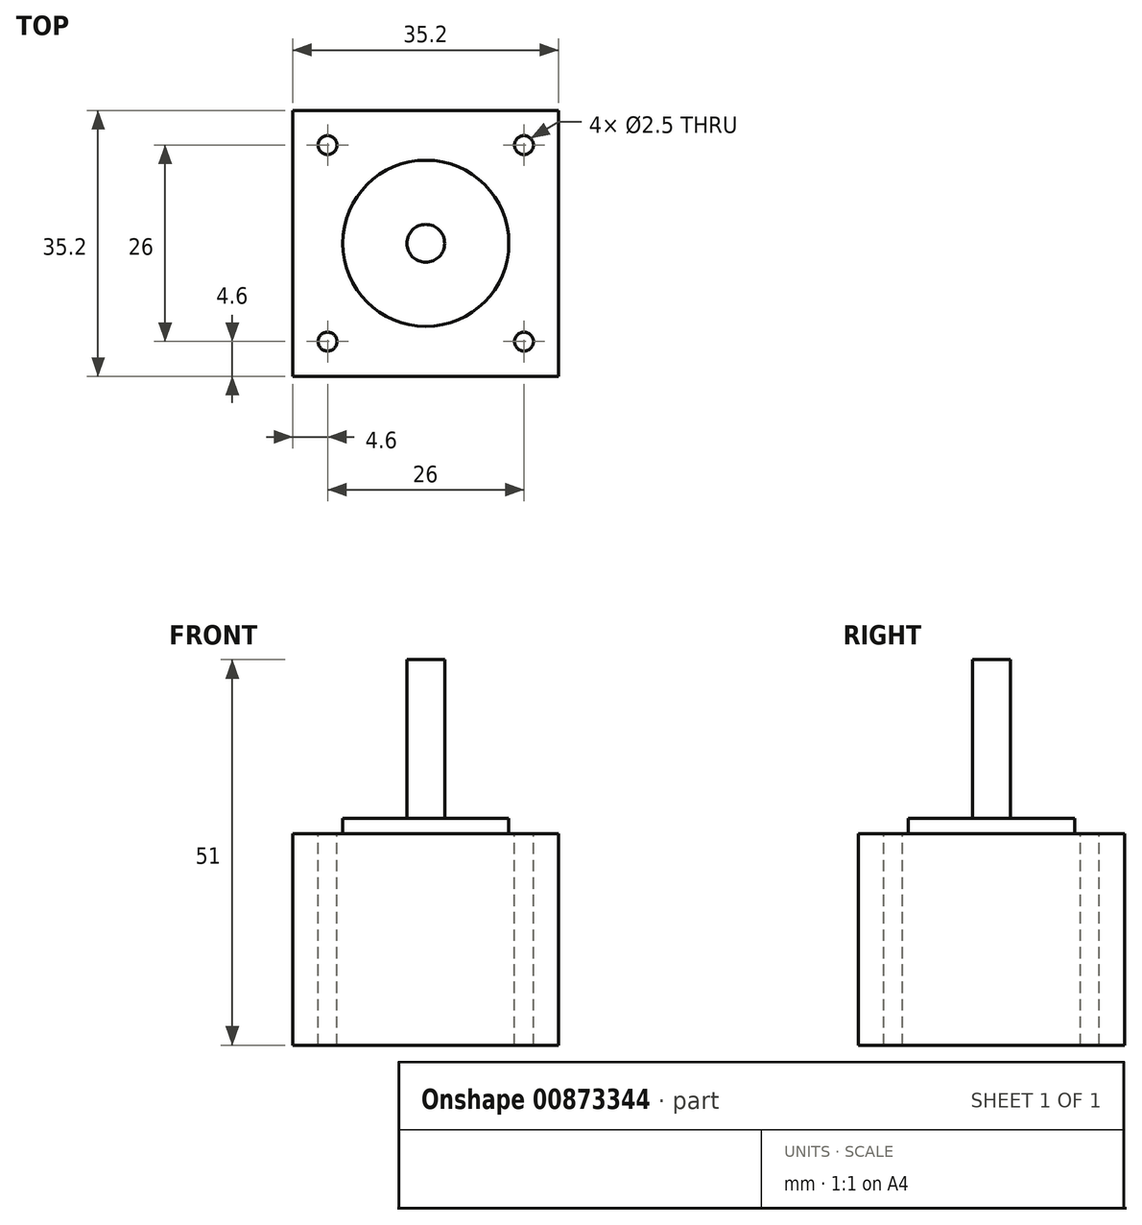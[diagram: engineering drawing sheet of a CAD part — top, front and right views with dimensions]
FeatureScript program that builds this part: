
annotation { "Feature Type Name" : "Feature", "Feature Type Description" : "" }
export const myFeature = defineFeature(function(context is Context, id is Id, definition is map)
    precondition{}
    {
        {
            var Q0;
            Q0=qCreatedBy(makeId("Top.planeOp"),FACE);
            var sketch = newSketch(context, id + "F0", { "sketchPlane" : qUnion([Q0])});
            skLineSegment(sketch, "E0.bottom", {"start": v(17.6, 17.6) * mm, "end": v(-17.6, 17.6) * mm});
            skLineSegment(sketch, "E0.top", {"start": v(17.6, -17.6) * mm, "end": v(-17.6, -17.6) * mm});
            skLineSegment(sketch, "E0.left", {"start": v(17.6, 17.6) * mm, "end": v(17.6, -17.6) * mm});
            skLineSegment(sketch, "E0.right", {"start": v(-17.6, 17.6) * mm, "end": v(-17.6, -17.6) * mm});
            skPoint(sketch, "E0.middle", {"position": v(0, 0) * mm});
            skSolve(sketch);
        }
        {
            var Q0;
            Q0=makeQuery(id+"F0.imprint","IMPRINT",FACE,{"disambiguationData":[TD([[makeQuery(id+"F0.imprint","IMPRINT",EDGE,{"derivedFrom":sQuery(id+"F0.wireOp",EDGE,"E0.bottom")}),1.0]])]});
            extrude(context, id + "F1", {"entities" : qUnion([Q0]), "depth" : 28 * mm, "offsetDistance" : 25 * mm});
        }
        {
            var Q0;
            Q0=makeQuery(id+"F1.opExtrude","CAP_FACE",FACE,{"disambiguationData":[OSD([sQuery(id+"F0.wireOp",EDGE,"E0.bottom"),sQuery(id+"F0.wireOp",EDGE,"E0.top"),sQuery(id+"F0.wireOp",EDGE,"E0.left"),sQuery(id+"F0.wireOp",EDGE,"E0.right")])],"isStart":false});
            var sketch = newSketch(context, id + "F2", { "sketchPlane" : qUnion([Q0])});
            skCircle(sketch, "E1", {"center": v(0, 0) * mm, "radius": 11 * mm});
            skSolve(sketch);
        }
        {
            var Q0;
            Q0=makeQuery(id+"F2.imprint","IMPRINT",FACE,{"disambiguationData":[TD([[makeQuery(id+"F2.imprint","IMPRINT",EDGE,{"derivedFrom":sQuery(id+"F2.wireOp",EDGE,"E1")}),1.0]])]});
            extrude(context, id + "F3", {"entities" : qUnion([Q0]), "operationType" : NewBodyOperationType.ADD, "depth" : 2 * mm, "offsetDistance" : 25 * mm});
        }
        {
            var Q0;
            Q0=makeQuery(id+"F3.opExtrude","CAP_FACE",FACE,{"disambiguationData":[OSD([sQuery(id+"F2.wireOp",EDGE,"E1")])],"isStart":false});
            var sketch = newSketch(context, id + "F4", { "sketchPlane" : qUnion([Q0])});
            skCircle(sketch, "E2", {"center": v(0, 0) * mm, "radius": 2.5 * mm});
            skSolve(sketch);
        }
        {
            var Q0;
            Q0=makeQuery(id+"F4.imprint","IMPRINT",FACE,{"disambiguationData":[TD([[makeQuery(id+"F4.imprint","IMPRINT",EDGE,{"derivedFrom":sQuery(id+"F4.wireOp",EDGE,"E2")}),1.0]])]});
            extrude(context, id + "F5", {"entities" : qUnion([Q0]), "operationType" : NewBodyOperationType.ADD, "depth" : 21 * mm, "offsetDistance" : 25 * mm});
        }
        {
            var Q0;
            Q0=makeQuery(id+"F1.opExtrude","CAP_FACE",FACE,{"disambiguationData":[OSD([sQuery(id+"F0.wireOp",EDGE,"E0.bottom"),sQuery(id+"F0.wireOp",EDGE,"E0.top"),sQuery(id+"F0.wireOp",EDGE,"E0.left"),sQuery(id+"F0.wireOp",EDGE,"E0.right")])],"isStart":false});
            var sketch = newSketch(context, id + "F6", { "sketchPlane" : qUnion([Q0])});
            skPoint(sketch, "E3", {"position": v(13, 13) * mm});
            skPoint(sketch, "E4", {"position": v(13, -13) * mm});
            skPoint(sketch, "E5", {"position": v(-13, -13) * mm});
            skPoint(sketch, "E6", {"position": v(-13, 13) * mm});
            skSolve(sketch);
        }
        {
            var Q0;
            Q0=sQuery(id+"F6.wireOp",VERTEX,"E3");
            var Q1;
            Q1=sQuery(id+"F6.wireOp",VERTEX,"E4");
            var Q2;
            Q2=sQuery(id+"F6.wireOp",VERTEX,"E5");
            var Q3;
            Q3=sQuery(id+"F6.wireOp",VERTEX,"E6");
            var Q4;
            Q4=makeQuery(id+"F1.opExtrude","SWEPT_BODY",BODY,{"disambiguationData":[OSD([sQuery(id+"F0.wireOp",EDGE,"E0.bottom"),sQuery(id+"F0.wireOp",EDGE,"E0.top"),sQuery(id+"F0.wireOp",EDGE,"E0.left"),sQuery(id+"F0.wireOp",EDGE,"E0.right")])]});
            hole(context, id + "F7", {"style" : HoleStyle.SIMPLE, "endStyle" : HoleEndStyle.THROUGH, "standardTappedOrClearance" : lookupTablePath({ "standard" : "ISO", "engagement" : "75%", "pitch" : "0.5 mm", "size" : "M3", "type" : "Tapped" }), "standardBlindInLast" : lookupTablePath({ "standard" : "ISO", "engagement" : "75%", "pitch" : "0.5 mm", "size" : "M3", "type" : "Tapped" }), "holeDiameter" : 2.5 * mm, "majorDiameter" : 3 * mm, "showTappedDepth" : true, "tappedDepth" : 3.5 * mm, "tapClearance" : 3, "locations" : qUnion([Q0, Q1, Q2, Q3]), "scope" : qUnion([Q4])});
        }
    });
